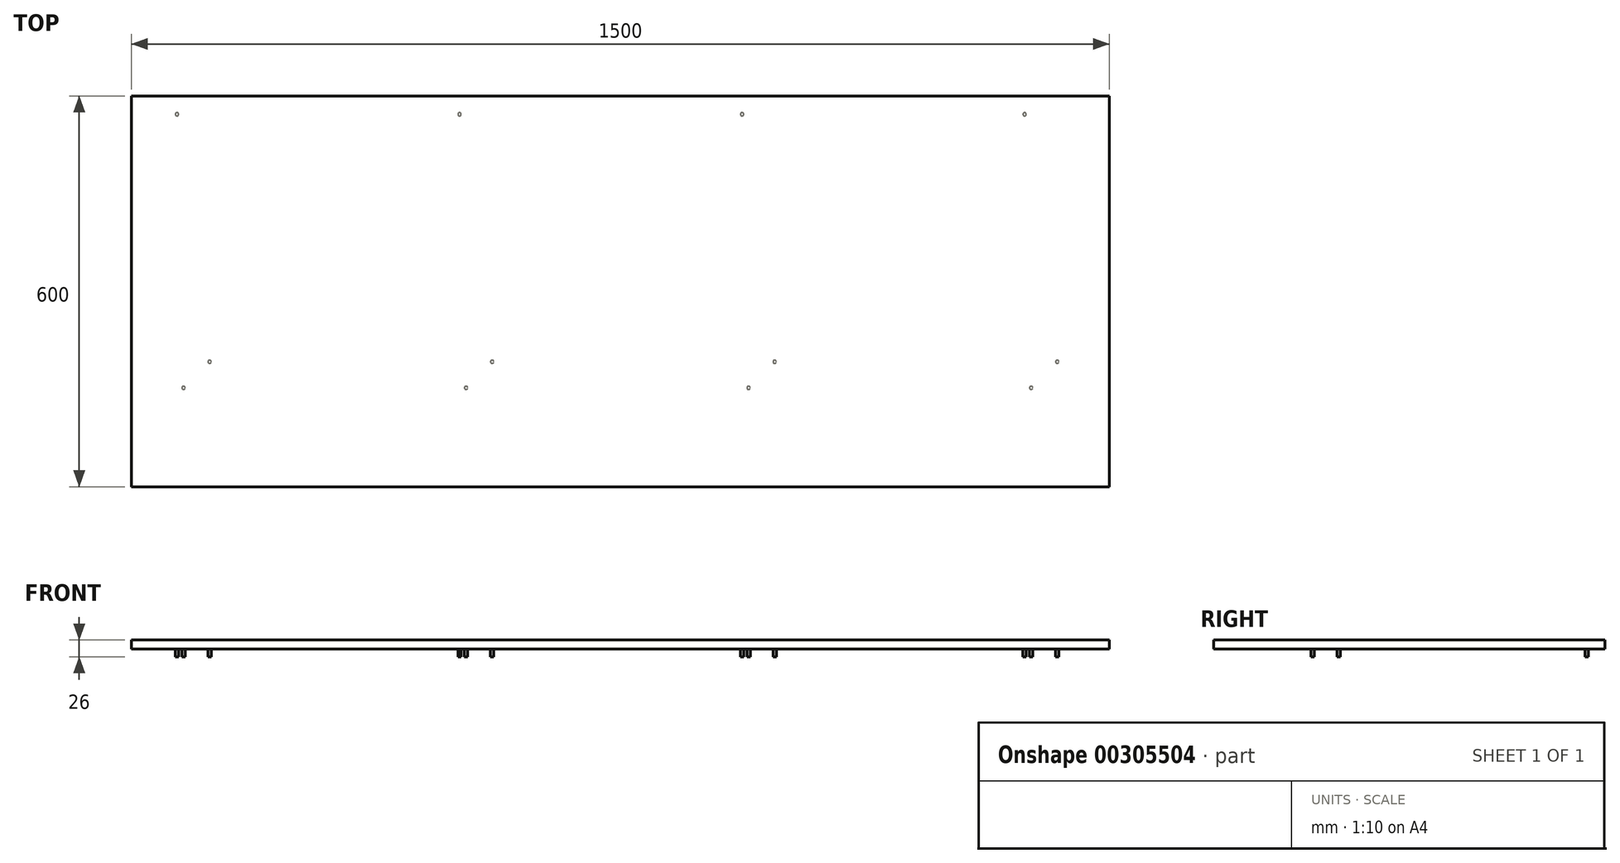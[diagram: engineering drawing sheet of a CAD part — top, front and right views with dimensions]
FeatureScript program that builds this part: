
annotation { "Feature Type Name" : "Feature", "Feature Type Description" : "" }
export const myFeature = defineFeature(function(context is Context, id is Id, definition is map)
    precondition{}
    {
        {
            var Q0;
            Q0=qCreatedBy(makeId("Right.planeOp"),FACE);
            var sketch = newSketch(context, id + "F0", { "sketchPlane" : qUnion([Q0])});
            skLineSegment(sketch, "E0.bottom", {"start": v(300, 13) * mm, "end": v(-300, 13) * mm});
            skLineSegment(sketch, "E0.top", {"start": v(300, -13) * mm, "end": v(-300, -13) * mm});
            skLineSegment(sketch, "E0.left", {"start": v(300, 13) * mm, "end": v(300, -13) * mm});
            skLineSegment(sketch, "E0.right", {"start": v(-300, 13) * mm, "end": v(-300, -13) * mm});
            skPoint(sketch, "E0.middle", {"position": v(0, 0) * mm});
            skSolve(sketch);
        }
        {
            var Q0;
            Q0=makeQuery(id+"F0.imprint","IMPRINT",FACE,{"disambiguationData":[TD([[makeQuery(id+"F0.imprint","IMPRINT",EDGE,{"derivedFrom":sQuery(id+"F0.wireOp",EDGE,"E0.bottom")}),1.0]])]});
            extrude(context, id + "F1", {"entities" : qUnion([Q0]), "endBound" : BoundingType.SYMMETRIC, "depth" : 1500 * mm});
        }
        {
            var Q0;
            Q0=makeQuery(id+"F1.opExtrude","SWEPT_FACE",FACE,{"disambiguationData":[OSD([sQuery(id+"F0.wireOp",EDGE,"E0.top")])]});
            var sketch = newSketch(context, id + "F2", { "sketchPlane" : qUnion([Q0])});
            skLineSegment(sketch, "E1", {"start": v(-750, -300) * mm, "end": v(-650, -300) * mm, "construction": true});
            skLineSegment(sketch, "E2", {"start": v(-650, -300) * mm, "end": v(-650, -272) * mm, "construction": true});
            skLineSegment(sketch, "E3", {"start": v(-650, -272) * mm, "end": v(-650, 128) * mm, "construction": true});
            skLineSegment(sketch, "E4", {"start": v(-650, 128) * mm, "end": v(-630, 128) * mm, "construction": true});
            skLineSegment(sketch, "E5", {"start": v(-630, 128) * mm, "end": v(-630, 148) * mm, "construction": true});
            skCircle(sketch, "E6", {"center": v(-630, 148) * mm, "radius": 2.5 * mm});
            skCircle(sketch, "E7.MirrorC", {"center": v(-670, 148) * mm, "radius": 2.5 * mm});
            skCircle(sketch, "E8.MirrorC", {"center": v(-670, 108) * mm, "radius": 2.5 * mm});
            skCircle(sketch, "E9.MirrorC", {"center": v(-630, 108) * mm, "radius": 2.5 * mm});
            skLineSegment(sketch, "E10", {"start": v(-650, -272) * mm, "end": v(-620, -272) * mm, "construction": true});
            skCircle(sketch, "E11", {"center": v(-620, -272) * mm, "radius": 2.5 * mm});
            skCircle(sketch, "E12.MirrorC", {"center": v(-680, -272) * mm, "radius": 2.5 * mm});
            skLineSegment(sketch, "E13.1.0.0", {"start": v(-216.67, -272) * mm, "end": v(-216.67, 128) * mm, "construction": true});
            skCircle(sketch, "E13.1.0.1", {"center": v(-246.67, -272) * mm, "radius": 2.5 * mm});
            skCircle(sketch, "E13.1.0.2", {"center": v(-196.67, 108) * mm, "radius": 2.5 * mm});
            skCircle(sketch, "E13.1.0.3", {"center": v(-236.67, 108) * mm, "radius": 2.5 * mm});
            skCircle(sketch, "E13.1.0.4", {"center": v(-236.67, 148) * mm, "radius": 2.5 * mm});
            skCircle(sketch, "E13.1.0.5", {"center": v(-186.67, -272) * mm, "radius": 2.5 * mm});
            skLineSegment(sketch, "E13.1.0.6", {"start": v(-216.67, -272) * mm, "end": v(-186.67, -272) * mm, "construction": true});
            skLineSegment(sketch, "E13.1.0.7", {"start": v(-216.67, -300) * mm, "end": v(-216.67, -272) * mm, "construction": true});
            skLineSegment(sketch, "E13.1.0.8", {"start": v(-216.67, 128) * mm, "end": v(-196.67, 128) * mm, "construction": true});
            skLineSegment(sketch, "E13.1.0.9", {"start": v(-196.67, 128) * mm, "end": v(-196.67, 148) * mm, "construction": true});
            skCircle(sketch, "E13.1.0.10", {"center": v(-196.67, 148) * mm, "radius": 2.5 * mm});
            skLineSegment(sketch, "E13.2.0.0", {"start": v(216.67, -272) * mm, "end": v(216.67, 128) * mm, "construction": true});
            skCircle(sketch, "E13.2.0.1", {"center": v(186.67, -272) * mm, "radius": 2.5 * mm});
            skCircle(sketch, "E13.2.0.2", {"center": v(236.67, 108) * mm, "radius": 2.5 * mm});
            skCircle(sketch, "E13.2.0.3", {"center": v(196.67, 108) * mm, "radius": 2.5 * mm});
            skCircle(sketch, "E13.2.0.4", {"center": v(196.67, 148) * mm, "radius": 2.5 * mm});
            skCircle(sketch, "E13.2.0.5", {"center": v(246.67, -272) * mm, "radius": 2.5 * mm});
            skLineSegment(sketch, "E13.2.0.6", {"start": v(216.67, -272) * mm, "end": v(246.67, -272) * mm, "construction": true});
            skLineSegment(sketch, "E13.2.0.7", {"start": v(216.67, -300) * mm, "end": v(216.67, -272) * mm, "construction": true});
            skLineSegment(sketch, "E13.2.0.8", {"start": v(216.67, 128) * mm, "end": v(236.67, 128) * mm, "construction": true});
            skLineSegment(sketch, "E13.2.0.9", {"start": v(236.67, 128) * mm, "end": v(236.67, 148) * mm, "construction": true});
            skCircle(sketch, "E13.2.0.10", {"center": v(236.67, 148) * mm, "radius": 2.5 * mm});
            skLineSegment(sketch, "E13.3.0.0", {"start": v(650, -272) * mm, "end": v(650, 128) * mm, "construction": true});
            skCircle(sketch, "E13.3.0.1", {"center": v(620, -272) * mm, "radius": 2.5 * mm});
            skCircle(sketch, "E13.3.0.2", {"center": v(670, 108) * mm, "radius": 2.5 * mm});
            skCircle(sketch, "E13.3.0.3", {"center": v(630, 108) * mm, "radius": 2.5 * mm});
            skCircle(sketch, "E13.3.0.4", {"center": v(630, 148) * mm, "radius": 2.5 * mm});
            skCircle(sketch, "E13.3.0.5", {"center": v(680, -272) * mm, "radius": 2.5 * mm});
            skLineSegment(sketch, "E13.3.0.6", {"start": v(650, -272) * mm, "end": v(680, -272) * mm, "construction": true});
            skLineSegment(sketch, "E13.3.0.7", {"start": v(650, -300) * mm, "end": v(650, -272) * mm, "construction": true});
            skLineSegment(sketch, "E13.3.0.8", {"start": v(650, 128) * mm, "end": v(670, 128) * mm, "construction": true});
            skLineSegment(sketch, "E13.3.0.9", {"start": v(670, 128) * mm, "end": v(670, 148) * mm, "construction": true});
            skCircle(sketch, "E13.3.0.10", {"center": v(670, 148) * mm, "radius": 2.5 * mm});
            skLineSegment(sketch, "E13.direction1", {"start": v(-650, -300) * mm, "end": v(-216.67, -300) * mm, "construction": true});
            skSolve(sketch);
        }
        {
            var Q0;
            Q0=makeQuery(id+"F2.imprint","IMPRINT",FACE,{"disambiguationData":[TD([[makeQuery(id+"F2.imprint","IMPRINT",EDGE,{"derivedFrom":sQuery(id+"F2.wireOp",EDGE,"E13.3.0.4")}),-1.0]])]});
            var Q1;
            Q1=makeQuery(id+"F2.imprint","IMPRINT",FACE,{"disambiguationData":[TD([[makeQuery(id+"F2.imprint","IMPRINT",EDGE,{"derivedFrom":sQuery(id+"F2.wireOp",EDGE,"E13.3.0.1")}),-1.0]])]});
            var Q2;
            Q2=makeQuery(id+"F2.imprint","IMPRINT",FACE,{"disambiguationData":[TD([[makeQuery(id+"F2.imprint","IMPRINT",EDGE,{"derivedFrom":sQuery(id+"F2.wireOp",EDGE,"E13.2.0.4")}),-1.0]])]});
            var Q3;
            Q3=makeQuery(id+"F2.imprint","IMPRINT",FACE,{"disambiguationData":[TD([[makeQuery(id+"F2.imprint","IMPRINT",EDGE,{"derivedFrom":sQuery(id+"F2.wireOp",EDGE,"E13.2.0.2")}),-1.0]])]});
            var Q4;
            Q4=makeQuery(id+"F2.imprint","IMPRINT",FACE,{"disambiguationData":[TD([[makeQuery(id+"F2.imprint","IMPRINT",EDGE,{"derivedFrom":sQuery(id+"F2.wireOp",EDGE,"E13.2.0.3")}),1.0]])]});
            var Q5;
            Q5=makeQuery(id+"F2.imprint","IMPRINT",FACE,{"disambiguationData":[TD([[makeQuery(id+"F2.imprint","IMPRINT",EDGE,{"derivedFrom":sQuery(id+"F2.wireOp",EDGE,"E7.MirrorC")}),-1.0]])]});
            var Q6;
            Q6=makeQuery(id+"F2.imprint","IMPRINT",FACE,{"disambiguationData":[TD([[makeQuery(id+"F2.imprint","IMPRINT",EDGE,{"derivedFrom":sQuery(id+"F2.wireOp",EDGE,"E8.MirrorC")}),1.0]])]});
            var Q7;
            Q7=makeQuery(id+"F2.imprint","IMPRINT",FACE,{"disambiguationData":[TD([[makeQuery(id+"F2.imprint","IMPRINT",EDGE,{"derivedFrom":sQuery(id+"F2.wireOp",EDGE,"E9.MirrorC")}),-1.0]])]});
            var Q8;
            Q8=makeQuery(id+"F2.imprint","IMPRINT",FACE,{"disambiguationData":[TD([[makeQuery(id+"F2.imprint","IMPRINT",EDGE,{"derivedFrom":sQuery(id+"F2.wireOp",EDGE,"E12.MirrorC")}),-1.0]])]});
            var Q9;
            Q9=makeQuery(id+"F2.imprint","IMPRINT",FACE,{"disambiguationData":[TD([[makeQuery(id+"F2.imprint","IMPRINT",EDGE,{"derivedFrom":sQuery(id+"F2.wireOp",EDGE,"E13.1.0.1")}),-1.0]])]});
            var Q10;
            Q10=makeQuery(id+"F2.imprint","IMPRINT",FACE,{"disambiguationData":[TD([[makeQuery(id+"F2.imprint","IMPRINT",EDGE,{"derivedFrom":sQuery(id+"F2.wireOp",EDGE,"E13.1.0.2")}),-1.0]])]});
            var Q11;
            Q11=makeQuery(id+"F2.imprint","IMPRINT",FACE,{"disambiguationData":[TD([[makeQuery(id+"F2.imprint","IMPRINT",EDGE,{"derivedFrom":sQuery(id+"F2.wireOp",EDGE,"E13.1.0.3")}),1.0]])]});
            var Q12;
            Q12=makeQuery(id+"F2.imprint","IMPRINT",FACE,{"disambiguationData":[TD([[makeQuery(id+"F2.imprint","IMPRINT",EDGE,{"derivedFrom":sQuery(id+"F2.wireOp",EDGE,"E13.1.0.4")}),-1.0]])]});
            var Q13;
            Q13=makeQuery(id+"F2.imprint","IMPRINT",FACE,{"disambiguationData":[TD([[makeQuery(id+"F2.imprint","IMPRINT",EDGE,{"derivedFrom":sQuery(id+"F2.wireOp",EDGE,"E13.2.0.1")}),-1.0]])]});
            var Q14;
            Q14=makeQuery(id+"F2.imprint","IMPRINT",FACE,{"disambiguationData":[TD([[makeQuery(id+"F2.imprint","IMPRINT",EDGE,{"derivedFrom":sQuery(id+"F2.wireOp",EDGE,"E13.3.0.2")}),-1.0]])]});
            var Q15;
            Q15=makeQuery(id+"F2.imprint","IMPRINT",FACE,{"disambiguationData":[TD([[makeQuery(id+"F2.imprint","IMPRINT",EDGE,{"derivedFrom":sQuery(id+"F2.wireOp",EDGE,"E13.3.0.3")}),1.0]])]});
            var Q16;
            Q16=makeQuery(id+"F2.imprint","IMPRINT",FACE,{"disambiguationData":[TD([[makeQuery(id+"F2.imprint","IMPRINT",EDGE,{"derivedFrom":sQuery(id+"F2.wireOp",EDGE,"E13.3.0.10")}),1.0]])]});
            var Q17;
            Q17=makeQuery(id+"F2.imprint","IMPRINT",FACE,{"disambiguationData":[TD([[makeQuery(id+"F2.imprint","IMPRINT",EDGE,{"derivedFrom":sQuery(id+"F2.wireOp",EDGE,"E13.2.0.10")}),1.0]])]});
            var Q18;
            Q18=makeQuery(id+"F2.imprint","IMPRINT",FACE,{"disambiguationData":[TD([[makeQuery(id+"F2.imprint","IMPRINT",EDGE,{"derivedFrom":sQuery(id+"F2.wireOp",EDGE,"E6")}),1.0]])]});
            var Q19;
            Q19=makeQuery(id+"F2.imprint","IMPRINT",FACE,{"disambiguationData":[TD([[makeQuery(id+"F2.imprint","IMPRINT",EDGE,{"derivedFrom":sQuery(id+"F2.wireOp",EDGE,"E11")}),1.0]])]});
            var Q20;
            Q20=makeQuery(id+"F2.imprint","IMPRINT",FACE,{"disambiguationData":[TD([[makeQuery(id+"F2.imprint","IMPRINT",EDGE,{"derivedFrom":sQuery(id+"F2.wireOp",EDGE,"E13.1.0.5")}),1.0]])]});
            var Q21;
            Q21=makeQuery(id+"F2.imprint","IMPRINT",FACE,{"disambiguationData":[TD([[makeQuery(id+"F2.imprint","IMPRINT",EDGE,{"derivedFrom":sQuery(id+"F2.wireOp",EDGE,"E13.1.0.10")}),1.0]])]});
            var Q22;
            Q22=makeQuery(id+"F2.imprint","IMPRINT",FACE,{"disambiguationData":[TD([[makeQuery(id+"F2.imprint","IMPRINT",EDGE,{"derivedFrom":sQuery(id+"F2.wireOp",EDGE,"E13.3.0.5")}),1.0]])]});
            var Q23;
            Q23=makeQuery(id+"F2.imprint","IMPRINT",FACE,{"disambiguationData":[TD([[makeQuery(id+"F2.imprint","IMPRINT",EDGE,{"derivedFrom":sQuery(id+"F2.wireOp",EDGE,"E13.2.0.5")}),1.0]])]});
            extrude(context, id + "F3", {"entities" : qUnion([Q0, Q1, Q2, Q3, Q4, Q5, Q6, Q7, Q8, Q9, Q10, Q11, Q12, Q13, Q14, Q15, Q16, Q17, Q18, Q19, Q20, Q21, Q22, Q23]), "operationType" : NewBodyOperationType.REMOVE, "oppositeDirection" : true, "depth" : 12 * mm});
        }
    });
